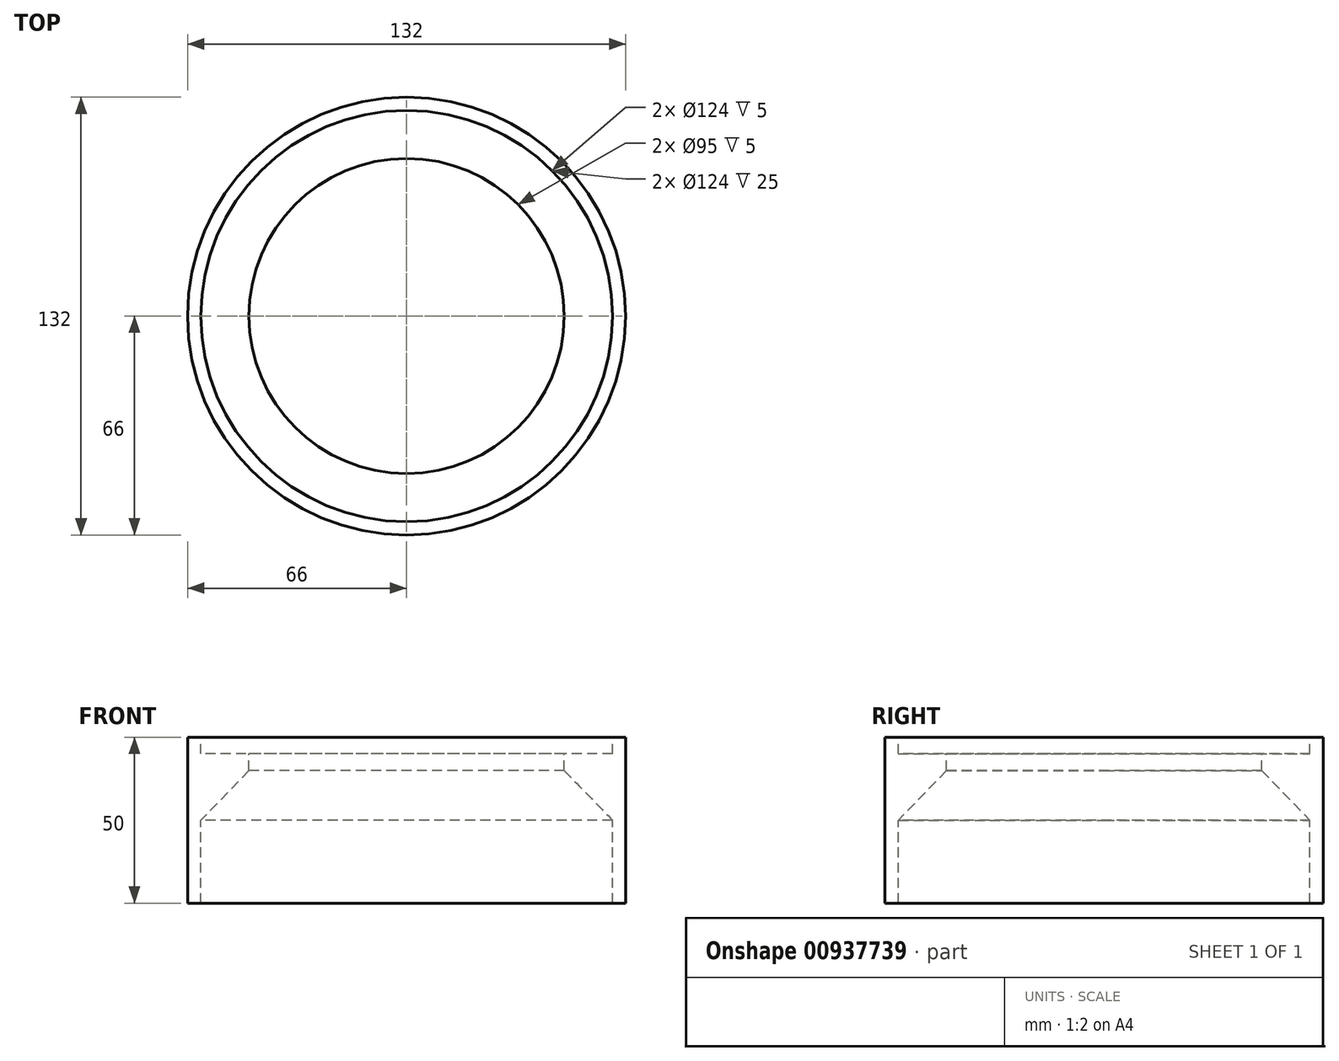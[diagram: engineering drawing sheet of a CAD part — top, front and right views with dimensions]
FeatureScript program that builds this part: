
annotation { "Feature Type Name" : "Feature", "Feature Type Description" : "" }
export const myFeature = defineFeature(function(context is Context, id is Id, definition is map)
    precondition{}
    {
        {
            var Q0;
            Q0=qCreatedBy(makeId("Front.planeOp"),FACE);
            var sketch = newSketch(context, id + "F0", { "sketchPlane" : qUnion([Q0])});
            skLineSegment(sketch, "E0", {"start": v(66, 0) * mm, "end": v(66, 50) * mm});
            skLineSegment(sketch, "E1", {"start": v(66, 50) * mm, "end": v(62, 50) * mm});
            skLineSegment(sketch, "E2", {"start": v(62, 50) * mm, "end": v(62, 45) * mm});
            skLineSegment(sketch, "E3", {"start": v(62, 45) * mm, "end": v(47.5, 45) * mm});
            skLineSegment(sketch, "E4", {"start": v(47.5, 45) * mm, "end": v(47.5, 40) * mm});
            skLineSegment(sketch, "E5", {"start": v(62, 0) * mm, "end": v(66, 0) * mm});
            skLineSegment(sketch, "E6", {"start": v(0, 70.32) * mm, "end": v(0, -47.87) * mm, "construction": true});
            skLineSegment(sketch, "E7", {"start": v(62, 0) * mm, "end": v(62, 25) * mm});
            skPoint(sketch, "E7.endSnap0", {"position": v(66, 25) * mm});
            skLineSegment(sketch, "E8", {"start": v(62, 25) * mm, "end": v(47.5, 40) * mm});
            skSolve(sketch);
        }
        {
            var Q0;
            Q0 = qSketchRegion(id + "F0", true);
            var Q1;
            Q1=sQuery(id+"F0.wireOp",EDGE,"E6");
            revolve(context, id + "F1", {"surfaceOperationType" : NewSurfaceOperationType.NEW, "entities" : qUnion([Q0]), "axis" : qUnion([Q1]), "revolveType" : RevolveType.FULL});
        }
    });
